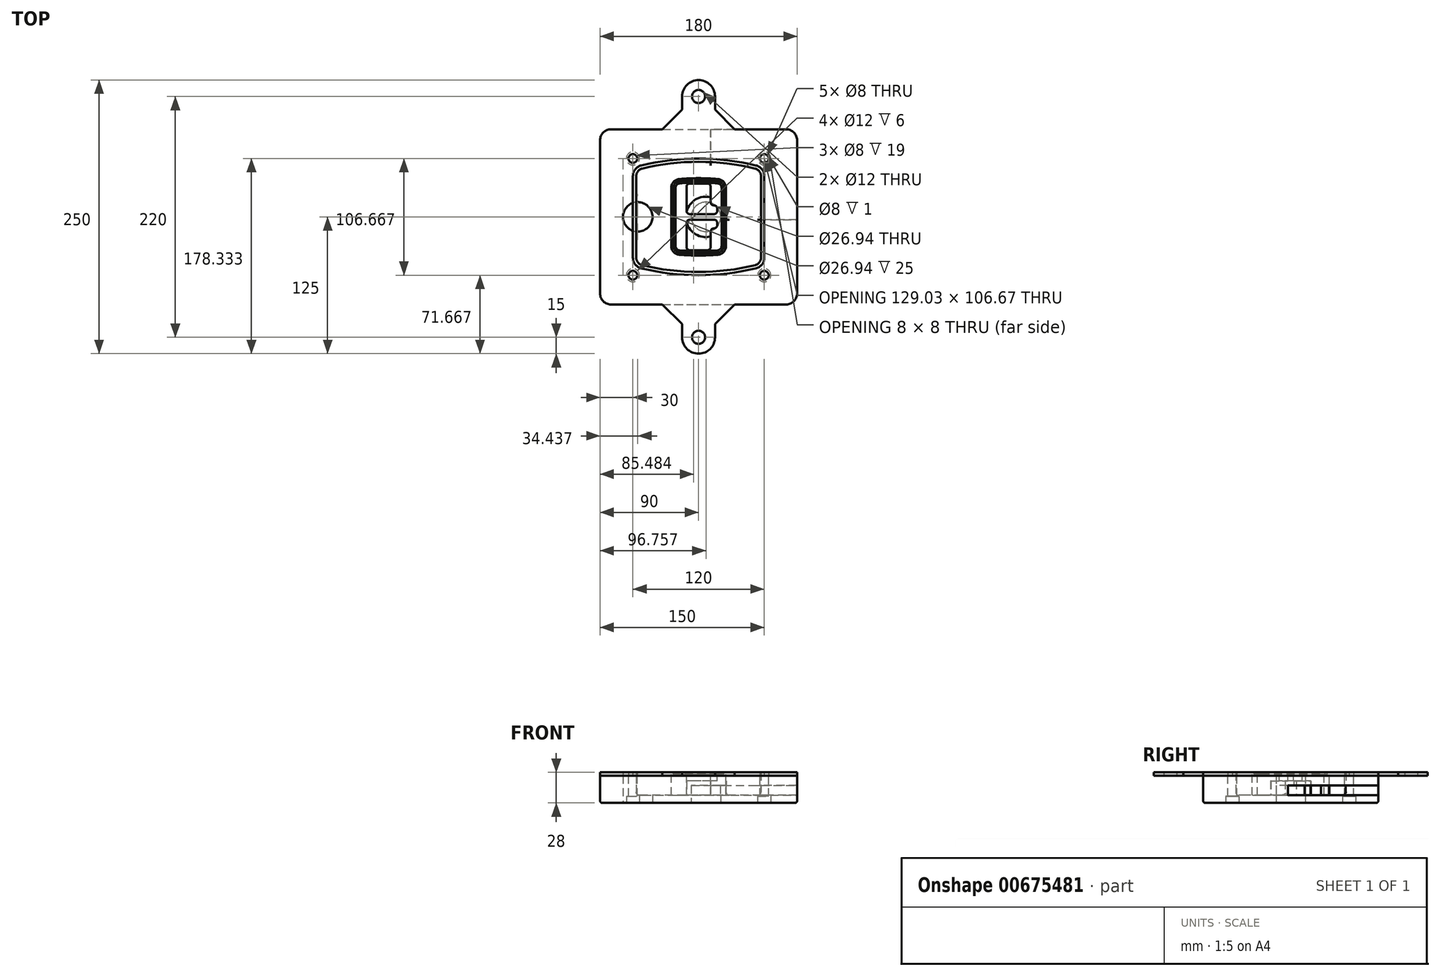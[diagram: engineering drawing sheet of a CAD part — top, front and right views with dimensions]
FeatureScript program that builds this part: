
annotation { "Feature Type Name" : "Feature", "Feature Type Description" : "" }
export const myFeature = defineFeature(function(context is Context, id is Id, definition is map)
    precondition{}
    {
        {
            var Q0;
            Q0=qCreatedBy(makeId("Top.planeOp"),FACE);
            var sketch = newSketch(context, id + "F0", { "sketchPlane" : qUnion([Q0])});
            skPoint(sketch, "E0.rect.middle", {"position": v(0, 0) * mm});
            skLineSegment(sketch, "E1.bottom", {"start": v(-80, -80) * mm, "end": v(80, -80) * mm});
            skLineSegment(sketch, "E1.top", {"start": v(-80, 80) * mm, "end": v(80, 80) * mm});
            skLineSegment(sketch, "E1.left", {"start": v(-90, -70) * mm, "end": v(-90, 70) * mm});
            skLineSegment(sketch, "E1.right", {"start": v(90, -70) * mm, "end": v(90, 70) * mm});
            skLineSegment(sketch, "E2", {"start": v(-90, 80) * mm, "end": v(90, -80) * mm, "construction": true});
            skLineSegment(sketch, "E3", {"start": v(90, 80) * mm, "end": v(-90, -80) * mm, "construction": true});
            skCircle(sketch, "E4", {"center": v(-60, 53.33) * mm, "radius": 4 * mm});
            skCircle(sketch, "E5", {"center": v(60, 53.33) * mm, "radius": 4 * mm});
            skCircle(sketch, "E6", {"center": v(60, -53.33) * mm, "radius": 4 * mm});
            skCircle(sketch, "E7", {"center": v(-60, -53.33) * mm, "radius": 4 * mm});
            skLineSegment(sketch, "E8", {"start": v(-60, 53.33) * mm, "end": v(60, 53.33) * mm, "construction": true});
            skLineSegment(sketch, "E9", {"start": v(60, 53.33) * mm, "end": v(60, -53.33) * mm, "construction": true});
            skLineSegment(sketch, "E10", {"start": v(60, -53.33) * mm, "end": v(-60, -53.33) * mm, "construction": true});
            skLineSegment(sketch, "E11", {"start": v(-60, -53.33) * mm, "end": v(-60, 53.33) * mm, "construction": true});
            skLineSegment(sketch, "E12", {"start": v(-60, 37.3) * mm, "end": v(-60, -37.3) * mm});
            skLineSegment(sketch, "E13", {"start": v(60, 37.3) * mm, "end": v(60, -37.3) * mm});
            skArc(sketch, "E14", {"start": v(52.38, 47.01) * mm, "mid": v(0, 53.33) * mm, "end": v(-52.38, 47.01) * mm});
            skArc(sketch, "E15", {"start": v(-52.38, -47.01) * mm, "mid": v(0, -53.33) * mm, "end": v(52.38, -47.01) * mm});
            skLineSegment(sketch, "E16", {"start": v(-60, 0) * mm, "end": v(60, 0) * mm, "construction": true});
            skPoint(sketch, "E17.visualSharp", {"position": v(-60, -45) * mm});
            skArc(sketch, "E17.filletArc", {"start": v(-60, -37.3) * mm, "mid": v(-57.87, -43.47) * mm, "end": v(-52.38, -47.01) * mm});
            skPoint(sketch, "E18.visualSharp", {"position": v(-60, 45) * mm});
            skArc(sketch, "E18.filletArc", {"start": v(-52.38, 47.01) * mm, "mid": v(-57.87, 43.47) * mm, "end": v(-60, 37.3) * mm});
            skPoint(sketch, "E19.visualSharp", {"position": v(60, 45) * mm});
            skArc(sketch, "E19.filletArc", {"start": v(60, 37.3) * mm, "mid": v(57.87, 43.47) * mm, "end": v(52.38, 47.01) * mm});
            skPoint(sketch, "E20.visualSharp", {"position": v(60, -45) * mm});
            skArc(sketch, "E20.filletArc", {"start": v(52.38, -47.01) * mm, "mid": v(57.87, -43.47) * mm, "end": v(60, -37.3) * mm});
            skPoint(sketch, "E21.visualSharp", {"position": v(-90, 80) * mm});
            skArc(sketch, "E21.filletArc", {"start": v(-80, 80) * mm, "mid": v(-87.07, 77.07) * mm, "end": v(-90, 70) * mm});
            skPoint(sketch, "E22.visualSharp", {"position": v(90, 80) * mm});
            skArc(sketch, "E22.filletArc", {"start": v(90, 70) * mm, "mid": v(87.07, 77.07) * mm, "end": v(80, 80) * mm});
            skPoint(sketch, "E23.visualSharp", {"position": v(90, -80) * mm});
            skArc(sketch, "E23.filletArc", {"start": v(80, -80) * mm, "mid": v(87.07, -77.07) * mm, "end": v(90, -70) * mm});
            skPoint(sketch, "E24.visualSharp", {"position": v(-90, -80) * mm});
            skArc(sketch, "E24.filletArc", {"start": v(-90, -70) * mm, "mid": v(-87.07, -77.07) * mm, "end": v(-80, -80) * mm});
            skArc(sketch, "E25.0", {"start": v(57, 37.3) * mm, "mid": v(55.5, 41.62) * mm, "end": v(51.67, 44.1) * mm});
            skLineSegment(sketch, "E25.1", {"start": v(57, 37.3) * mm, "end": v(57, -37.3) * mm});
            skArc(sketch, "E25.2", {"start": v(51.67, -44.1) * mm, "mid": v(55.5, -41.62) * mm, "end": v(57, -37.3) * mm});
            skArc(sketch, "E25.3", {"start": v(-51.67, -44.1) * mm, "mid": v(0, -50.33) * mm, "end": v(51.67, -44.1) * mm});
            skArc(sketch, "E25.4", {"start": v(-57, -37.3) * mm, "mid": v(-55.5, -41.62) * mm, "end": v(-51.67, -44.1) * mm});
            skArc(sketch, "E25.5", {"start": v(51.67, 44.1) * mm, "mid": v(0, 50.33) * mm, "end": v(-51.67, 44.1) * mm});
            skLineSegment(sketch, "E25.6", {"start": v(-57, 37.3) * mm, "end": v(-57, -37.3) * mm});
            skArc(sketch, "E25.7", {"start": v(-51.67, 44.1) * mm, "mid": v(-55.5, 41.62) * mm, "end": v(-57, 37.3) * mm});
            skArc(sketch, "E26.0", {"start": v(-53.33, 50.9) * mm, "mid": v(-61.01, 45.94) * mm, "end": v(-64, 37.3) * mm});
            skArc(sketch, "E26.1", {"start": v(53.33, 50.9) * mm, "mid": v(0, 57.33) * mm, "end": v(-53.33, 50.9) * mm});
            skArc(sketch, "E26.2", {"start": v(64, 37.3) * mm, "mid": v(61.01, 45.94) * mm, "end": v(53.33, 50.9) * mm});
            skLineSegment(sketch, "E26.3", {"start": v(64, 37.3) * mm, "end": v(64, -37.3) * mm});
            skArc(sketch, "E26.4", {"start": v(53.33, -50.9) * mm, "mid": v(61.01, -45.94) * mm, "end": v(64, -37.3) * mm});
            skLineSegment(sketch, "E26.5", {"start": v(-64, 37.3) * mm, "end": v(-64, -37.3) * mm});
            skArc(sketch, "E26.6", {"start": v(-53.33, -50.9) * mm, "mid": v(0, -57.33) * mm, "end": v(53.33, -50.9) * mm});
            skArc(sketch, "E26.7", {"start": v(-64, -37.3) * mm, "mid": v(-61.01, -45.94) * mm, "end": v(-53.33, -50.9) * mm});
            skSolve(sketch);
        }
        {
            var Q0;
            Q0=makeQuery(id+"F0.imprint","IMPRINT",FACE,{"disambiguationData":[TD([[makeQuery(id+"F0.imprint","IMPRINT",EDGE,{"derivedFrom":sQuery(id+"F0.wireOp",EDGE,"E1.bottom")}),1.0]])]});
            var Q1;
            Q1=makeQuery(id+"F0.imprint","IMPRINT",FACE,{"disambiguationData":[TD([[makeQuery(id+"F0.imprint","IMPRINT",EDGE,{"derivedFrom":sQuery(id+"F0.wireOp",EDGE,"E12")}),1.0]])]});
            var Q2;
            Q2=makeQuery(id+"F0.imprint","IMPRINT",FACE,{"disambiguationData":[TD([[makeQuery(id+"F0.imprint","IMPRINT",EDGE,{"derivedFrom":sQuery(id+"F0.wireOp",EDGE,"E25.0")}),1.0]])]});
            var Q3;
            Q3=makeQuery(id+"F0.imprint","IMPRINT",FACE,{"disambiguationData":[TD([[makeQuery(id+"F0.imprint","IMPRINT",EDGE,{"derivedFrom":sQuery(id+"F0.wireOp",EDGE,"E12")}),-1.0]])]});
            extrude(context, id + "F1", {"entities" : qUnion([Q0, Q1, Q2, Q3]), "oppositeDirection" : true, "depth" : 25 * mm});
        }
        {
            var Q0;
            Q0=makeQuery(id+"F0.imprint","IMPRINT",FACE,{"disambiguationData":[TD([[makeQuery(id+"F0.imprint","IMPRINT",EDGE,{"derivedFrom":sQuery(id+"F0.wireOp",EDGE,"E12")}),1.0]])]});
            extrude(context, id + "F2", {"entities" : qUnion([Q0]), "operationType" : NewBodyOperationType.ADD, "depth" : 3 * mm});
        }
        {
            var Q0;
            Q0=makeQuery(id+"F0.imprint","IMPRINT",FACE,{"disambiguationData":[TD([[makeQuery(id+"F0.imprint","IMPRINT",EDGE,{"derivedFrom":sQuery(id+"F0.wireOp",EDGE,"E25.0")}),1.0]])]});
            extrude(context, id + "F3", {"entities" : qUnion([Q0]), "operationType" : NewBodyOperationType.REMOVE, "oppositeDirection" : true, "depth" : 18 * mm});
        }
        {
            var Q0;
            Q0=makeQuery(id+"F2.opExtrude","CAP_FACE",FACE,{"disambiguationData":[OSD([sQuery(id+"F0.wireOp",EDGE,"E12"),sQuery(id+"F0.wireOp",EDGE,"E13"),sQuery(id+"F0.wireOp",EDGE,"E14"),sQuery(id+"F0.wireOp",EDGE,"E15"),sQuery(id+"F0.wireOp",EDGE,"E17.filletArc"),sQuery(id+"F0.wireOp",EDGE,"E18.filletArc"),sQuery(id+"F0.wireOp",EDGE,"E19.filletArc"),sQuery(id+"F0.wireOp",EDGE,"E20.filletArc"),sQuery(id+"F0.wireOp",EDGE,"E25.0"),sQuery(id+"F0.wireOp",EDGE,"E25.1"),sQuery(id+"F0.wireOp",EDGE,"E25.2"),sQuery(id+"F0.wireOp",EDGE,"E25.3"),sQuery(id+"F0.wireOp",EDGE,"E25.4"),sQuery(id+"F0.wireOp",EDGE,"E25.5"),sQuery(id+"F0.wireOp",EDGE,"E25.6"),sQuery(id+"F0.wireOp",EDGE,"E25.7")])],"isStart":false});
            var sketch = newSketch(context, id + "F4", { "sketchPlane" : qUnion([Q0])});
            skArc(sketch, "E27.0", {"start": v(-17.7, -34.56) * mm, "mid": v(0, -35.33) * mm, "end": v(17.7, -34.56) * mm});
            skArc(sketch, "E28.0", {"start": v(17.7, 34.56) * mm, "mid": v(0, 35.33) * mm, "end": v(-17.7, 34.56) * mm});
            skLineSegment(sketch, "E29", {"start": v(-25, 26.59) * mm, "end": v(-25, -26.59) * mm});
            skLineSegment(sketch, "E30", {"start": v(25, 26.59) * mm, "end": v(25, -26.59) * mm});
            skLineSegment(sketch, "E31", {"start": v(-25, 33.78) * mm, "end": v(25, 33.78) * mm, "construction": true});
            skLineSegment(sketch, "E32", {"start": v(-25, -33.78) * mm, "end": v(25, -33.78) * mm, "construction": true});
            skPoint(sketch, "E33.visualSharp", {"position": v(-25, 33.78) * mm});
            skArc(sketch, "E33.filletArc", {"start": v(-17.7, 34.56) * mm, "mid": v(-22.9, 32) * mm, "end": v(-25, 26.59) * mm});
            skPoint(sketch, "E34.visualSharp", {"position": v(25, 33.78) * mm});
            skArc(sketch, "E34.filletArc", {"start": v(25, 26.59) * mm, "mid": v(22.9, 32) * mm, "end": v(17.7, 34.56) * mm});
            skPoint(sketch, "E35.visualSharp", {"position": v(25, -33.78) * mm});
            skArc(sketch, "E35.filletArc", {"start": v(17.7, -34.56) * mm, "mid": v(22.9, -32) * mm, "end": v(25, -26.59) * mm});
            skPoint(sketch, "E36.visualSharp", {"position": v(-25, -33.78) * mm});
            skArc(sketch, "E36.filletArc", {"start": v(-25, -26.59) * mm, "mid": v(-22.9, -32) * mm, "end": v(-17.7, -34.56) * mm});
            skArc(sketch, "E37.0", {"start": v(51.67, 44.1) * mm, "mid": v(0, 50.33) * mm, "end": v(-51.67, 44.1) * mm});
            skArc(sketch, "E37.1", {"start": v(-51.67, 44.1) * mm, "mid": v(-55.5, 41.62) * mm, "end": v(-57, 37.3) * mm});
            skLineSegment(sketch, "E37.2", {"start": v(-57, 37.3) * mm, "end": v(-57, -37.3) * mm});
            skArc(sketch, "E37.3", {"start": v(-57, -37.3) * mm, "mid": v(-55.5, -41.62) * mm, "end": v(-51.67, -44.1) * mm});
            skArc(sketch, "E37.4", {"start": v(-51.67, -44.1) * mm, "mid": v(0, -50.33) * mm, "end": v(51.67, -44.1) * mm});
            skArc(sketch, "E37.5", {"start": v(51.67, -44.1) * mm, "mid": v(55.5, -41.62) * mm, "end": v(57, -37.3) * mm});
            skLineSegment(sketch, "E37.6", {"start": v(57, 37.3) * mm, "end": v(57, -37.3) * mm});
            skArc(sketch, "E37.7", {"start": v(57, 37.3) * mm, "mid": v(55.5, 41.62) * mm, "end": v(51.67, 44.1) * mm});
            skLineSegment(sketch, "E38.0", {"start": v(23, 26.59) * mm, "end": v(23, -26.59) * mm});
            skArc(sketch, "E38.1", {"start": v(17.53, -32.56) * mm, "mid": v(21.42, -30.64) * mm, "end": v(23, -26.59) * mm});
            skArc(sketch, "E38.2", {"start": v(-17.53, -32.56) * mm, "mid": v(0, -33.33) * mm, "end": v(17.53, -32.56) * mm});
            skArc(sketch, "E38.3", {"start": v(-23, -26.59) * mm, "mid": v(-21.42, -30.64) * mm, "end": v(-17.53, -32.56) * mm});
            skLineSegment(sketch, "E38.4", {"start": v(-23, 26.59) * mm, "end": v(-23, -26.59) * mm});
            skArc(sketch, "E38.5", {"start": v(23, 26.59) * mm, "mid": v(21.42, 30.64) * mm, "end": v(17.53, 32.56) * mm});
            skArc(sketch, "E38.6", {"start": v(-17.53, 32.56) * mm, "mid": v(-21.42, 30.64) * mm, "end": v(-23, 26.59) * mm});
            skArc(sketch, "E38.7", {"start": v(17.53, 32.56) * mm, "mid": v(0, 33.33) * mm, "end": v(-17.53, 32.56) * mm});
            skArc(sketch, "E39.0", {"start": v(21, 26.59) * mm, "mid": v(19.95, 29.29) * mm, "end": v(17.35, 30.57) * mm});
            skLineSegment(sketch, "E39.1", {"start": v(21, 26.59) * mm, "end": v(21, -26.59) * mm});
            skArc(sketch, "E39.2", {"start": v(17.35, -30.57) * mm, "mid": v(19.95, -29.29) * mm, "end": v(21, -26.59) * mm});
            skArc(sketch, "E39.3", {"start": v(-17.35, -30.57) * mm, "mid": v(0, -31.33) * mm, "end": v(17.35, -30.57) * mm});
            skArc(sketch, "E39.4", {"start": v(-21, -26.59) * mm, "mid": v(-19.95, -29.29) * mm, "end": v(-17.35, -30.57) * mm});
            skArc(sketch, "E39.5", {"start": v(17.35, 30.57) * mm, "mid": v(0, 31.33) * mm, "end": v(-17.35, 30.57) * mm});
            skLineSegment(sketch, "E39.6", {"start": v(-21, 26.59) * mm, "end": v(-21, -26.59) * mm});
            skArc(sketch, "E39.7", {"start": v(-17.35, 30.57) * mm, "mid": v(-19.95, 29.29) * mm, "end": v(-21, 26.59) * mm});
            skLineSegment(sketch, "E40", {"start": v(-25, 0) * mm, "end": v(25, 0) * mm, "construction": true});
            skLineSegment(sketch, "E41", {"start": v(-11, 5.5) * mm, "end": v(-11, 27.5) * mm});
            skLineSegment(sketch, "E42", {"start": v(-8, 30.5) * mm, "end": v(8, 30.5) * mm});
            skLineSegment(sketch, "E43", {"start": v(11, 27.5) * mm, "end": v(11, 13.5) * mm});
            skLineSegment(sketch, "E44", {"start": v(14, 10.5) * mm, "end": v(14, 10.5) * mm});
            skLineSegment(sketch, "E45", {"start": v(17, 7.5) * mm, "end": v(17, 5.5) * mm});
            skLineSegment(sketch, "E46", {"start": v(14, 2.5) * mm, "end": v(-8, 2.5) * mm});
            skPoint(sketch, "E47.visualSharp", {"position": v(-11, 30.5) * mm});
            skArc(sketch, "E47.filletArc", {"start": v(-8, 30.5) * mm, "mid": v(-10.12, 29.62) * mm, "end": v(-11, 27.5) * mm});
            skPoint(sketch, "E48.visualSharp", {"position": v(11, 30.5) * mm});
            skArc(sketch, "E48.filletArc", {"start": v(11, 27.5) * mm, "mid": v(10.12, 29.62) * mm, "end": v(8, 30.5) * mm});
            skPoint(sketch, "E49.visualSharp", {"position": v(11, 10.5) * mm});
            skArc(sketch, "E49.filletArc", {"start": v(11, 13.5) * mm, "mid": v(11.88, 11.38) * mm, "end": v(14, 10.5) * mm});
            skPoint(sketch, "E50.visualSharp", {"position": v(17, 10.5) * mm});
            skArc(sketch, "E50.filletArc", {"start": v(17, 7.5) * mm, "mid": v(16.12, 9.62) * mm, "end": v(14, 10.5) * mm});
            skPoint(sketch, "E51.visualSharp", {"position": v(17, 2.5) * mm});
            skArc(sketch, "E51.filletArc", {"start": v(14, 2.5) * mm, "mid": v(16.12, 3.38) * mm, "end": v(17, 5.5) * mm});
            skPoint(sketch, "E52.visualSharp", {"position": v(-11, 2.5) * mm});
            skArc(sketch, "E52.filletArc", {"start": v(-11, 5.5) * mm, "mid": v(-10.12, 3.38) * mm, "end": v(-8, 2.5) * mm});
            skLineSegment(sketch, "E53.0.MirrorCS", {"start": v(14, -2.5) * mm, "end": v(-8, -2.5) * mm});
            skArc(sketch, "E54.0.MirrorCS", {"start": v(-11, -5.5) * mm, "mid": v(-10.12, -3.38) * mm, "end": v(-8, -2.5) * mm});
            skLineSegment(sketch, "E55.0.MirrorCS", {"start": v(-11, -5.5) * mm, "end": v(-11, -27.5) * mm});
            skArc(sketch, "E56.0.MirrorCS", {"start": v(-8, -30.5) * mm, "mid": v(-10.12, -29.62) * mm, "end": v(-11, -27.5) * mm});
            skLineSegment(sketch, "E57.0.MirrorCS", {"start": v(-8, -30.5) * mm, "end": v(8, -30.5) * mm});
            skArc(sketch, "E58.0.MirrorCS", {"start": v(11, -27.5) * mm, "mid": v(10.12, -29.62) * mm, "end": v(8, -30.5) * mm});
            skLineSegment(sketch, "E59.0.MirrorCS", {"start": v(11, -27.5) * mm, "end": v(11, -13.5) * mm});
            skArc(sketch, "E60.0.MirrorCS", {"start": v(11, -13.5) * mm, "mid": v(11.88, -11.38) * mm, "end": v(14, -10.5) * mm});
            skArc(sketch, "E61.0.MirrorCS", {"start": v(17, -7.5) * mm, "mid": v(16.12, -9.62) * mm, "end": v(14, -10.5) * mm});
            skLineSegment(sketch, "E62.0.MirrorCS", {"start": v(17, -7.5) * mm, "end": v(17, -5.5) * mm});
            skArc(sketch, "E63.0.MirrorCS", {"start": v(14, -2.5) * mm, "mid": v(16.12, -3.38) * mm, "end": v(17, -5.5) * mm});
            skSolve(sketch);
        }
        {
            var Q0;
            Q0=makeQuery(id+"F4.imprint","IMPRINT",FACE,{"disambiguationData":[TD([[makeQuery(id+"F4.imprint","IMPRINT",EDGE,{"derivedFrom":sQuery(id+"F4.wireOp",EDGE,"E27.0")}),1.0]])]});
            var Q1;
            Q1=makeQuery(id+"F4.imprint","IMPRINT",FACE,{"disambiguationData":[TD([[makeQuery(id+"F4.imprint","IMPRINT",EDGE,{"derivedFrom":sQuery(id+"F4.wireOp",EDGE,"E38.0")}),-1.0]])]});
            var Q2;
            Q2=makeQuery(id+"F4.imprint","IMPRINT",FACE,{"disambiguationData":[TD([[makeQuery(id+"F4.imprint","IMPRINT",EDGE,{"derivedFrom":sQuery(id+"F4.wireOp",EDGE,"E39.0")}),1.0]])]});
            extrude(context, id + "F5", {"entities" : qUnion([Q0, Q1, Q2]), "operationType" : NewBodyOperationType.ADD, "endBound" : BoundingType.UP_TO_NEXT, "oppositeDirection" : true, "depth" : 25 * mm});
        }
        {
            var Q0;
            Q0=makeQuery(id+"F4.imprint","IMPRINT",FACE,{"disambiguationData":[TD([[makeQuery(id+"F4.imprint","IMPRINT",EDGE,{"derivedFrom":sQuery(id+"F4.wireOp",EDGE,"E38.0")}),-1.0]])]});
            extrude(context, id + "F6", {"entities" : qUnion([Q0]), "operationType" : NewBodyOperationType.REMOVE, "oppositeDirection" : true, "depth" : 2 * mm});
        }
        {
            var Q0;
            Q0=makeQuery(id+"F1.opExtrude","CAP_FACE",FACE,{"disambiguationData":[OSD([sQuery(id+"F0.wireOp",EDGE,"E1.bottom"),sQuery(id+"F0.wireOp",EDGE,"E1.top"),sQuery(id+"F0.wireOp",EDGE,"E1.left"),sQuery(id+"F0.wireOp",EDGE,"E1.right"),sQuery(id+"F0.wireOp",EDGE,"E4"),sQuery(id+"F0.wireOp",EDGE,"E5"),sQuery(id+"F0.wireOp",EDGE,"E6"),sQuery(id+"F0.wireOp",EDGE,"E7"),sQuery(id+"F0.wireOp",EDGE,"E21.filletArc"),sQuery(id+"F0.wireOp",EDGE,"E22.filletArc"),sQuery(id+"F0.wireOp",EDGE,"E23.filletArc"),sQuery(id+"F0.wireOp",EDGE,"E24.filletArc")])],"isStart":false});
            var sketch = newSketch(context, id + "F7", { "sketchPlane" : qUnion([Q0])});
            skCircle(sketch, "E64", {"center": v(6.76, 0) * mm, "radius": 13.47 * mm});
            skCircle(sketch, "E65", {"center": v(-55.56, 0) * mm, "radius": 13.47 * mm});
            skLineSegment(sketch, "E66", {"start": v(90, 0) * mm, "end": v(-90, 0) * mm});
            skCircle(sketch, "E67", {"center": v(6.76, 0) * mm, "radius": 18.47 * mm});
            skCircle(sketch, "E68", {"center": v(60, -53.33) * mm, "radius": 6 * mm});
            skCircle(sketch, "E69", {"center": v(-60, -53.33) * mm, "radius": 6 * mm});
            skCircle(sketch, "E70", {"center": v(-60, 53.33) * mm, "radius": 6 * mm});
            skCircle(sketch, "E71", {"center": v(60, 53.33) * mm, "radius": 6 * mm});
            skSolve(sketch);
        }
        {
            var Q0;
            {var subQ1=sQuery(id+"F7.wireOp",EDGE,"E66");var subQ4=sQuery(id+"F7.wireOp",EDGE,"E64");var subQ6=makeQuery(id+"F7.imprint","INTERSECT",VERTEX,{"disambiguationData":[OD(0.0)],"derivedFrom":[subQ4,subQ1]});Q0=makeQuery(id+"F7.imprint","IMPRINT",FACE,{"disambiguationData":[TD([[makeQuery(id+"F7.imprint","IMPRINT",EDGE,{"disambiguationData":[TD([[subQ6,-1.0]])],"derivedFrom":subQ4}),-1.0]])]});}
            var Q1;
            {var subQ0=sQuery(id+"F7.wireOp",EDGE,"E66");var subQ1=sQuery(id+"F7.wireOp",EDGE,"E64");var subQ3=makeQuery(id+"F7.imprint","INTERSECT",VERTEX,{"disambiguationData":[OD(0.0)],"derivedFrom":[subQ1,subQ0]});Q1=makeQuery(id+"F7.imprint","IMPRINT",FACE,{"disambiguationData":[TD([[makeQuery(id+"F7.imprint","IMPRINT",EDGE,{"disambiguationData":[TD([[subQ3,-1.0]])],"derivedFrom":subQ1}),1.0]])]});}
            var Q2;
            {var subQ0=sQuery(id+"F7.wireOp",EDGE,"E66");var subQ1=sQuery(id+"F7.wireOp",EDGE,"E64");var subQ3=makeQuery(id+"F7.imprint","INTERSECT",VERTEX,{"disambiguationData":[OD(0.0)],"derivedFrom":[subQ1,subQ0]});Q2=makeQuery(id+"F7.imprint","IMPRINT",FACE,{"disambiguationData":[TD([[makeQuery(id+"F7.imprint","IMPRINT",EDGE,{"disambiguationData":[TD([[subQ3,1.0]])],"derivedFrom":subQ1}),1.0]])]});}
            var Q3;
            {var subQ1=sQuery(id+"F7.wireOp",EDGE,"E66");var subQ4=sQuery(id+"F7.wireOp",EDGE,"E64");var subQ6=makeQuery(id+"F7.imprint","INTERSECT",VERTEX,{"disambiguationData":[OD(0.0)],"derivedFrom":[subQ4,subQ1]});Q3=makeQuery(id+"F7.imprint","IMPRINT",FACE,{"disambiguationData":[TD([[makeQuery(id+"F7.imprint","IMPRINT",EDGE,{"disambiguationData":[TD([[subQ6,1.0]])],"derivedFrom":subQ4}),-1.0]])]});}
            extrude(context, id + "F8", {"entities" : qUnion([Q0, Q1, Q2, Q3]), "operationType" : NewBodyOperationType.ADD, "oppositeDirection" : true, "depth" : 20 * mm});
        }
        {
            var Q0;
            {var subQ0=sQuery(id+"F7.wireOp",EDGE,"E66");var subQ1=sQuery(id+"F7.wireOp",EDGE,"E64");var subQ3=makeQuery(id+"F7.imprint","INTERSECT",VERTEX,{"disambiguationData":[OD(0.0)],"derivedFrom":[subQ1,subQ0]});Q0=makeQuery(id+"F7.imprint","IMPRINT",FACE,{"disambiguationData":[TD([[makeQuery(id+"F7.imprint","IMPRINT",EDGE,{"disambiguationData":[TD([[subQ3,-1.0]])],"derivedFrom":subQ1}),1.0]])]});}
            var Q1;
            {var subQ0=sQuery(id+"F7.wireOp",EDGE,"E66");var subQ1=sQuery(id+"F7.wireOp",EDGE,"E64");var subQ3=makeQuery(id+"F7.imprint","INTERSECT",VERTEX,{"disambiguationData":[OD(0.0)],"derivedFrom":[subQ1,subQ0]});Q1=makeQuery(id+"F7.imprint","IMPRINT",FACE,{"disambiguationData":[TD([[makeQuery(id+"F7.imprint","IMPRINT",EDGE,{"disambiguationData":[TD([[subQ3,1.0]])],"derivedFrom":subQ1}),1.0]])]});}
            extrude(context, id + "F9", {"entities" : qUnion([Q0, Q1]), "operationType" : NewBodyOperationType.REMOVE, "oppositeDirection" : true, "depth" : 16 * mm});
        }
        {
            var Q0;
            {var subQ0=sQuery(id+"F7.wireOp",EDGE,"E66");var subQ1=sQuery(id+"F7.wireOp",EDGE,"E65");var subQ3=makeQuery(id+"F7.imprint","INTERSECT",VERTEX,{"disambiguationData":[OD(0.0)],"derivedFrom":[subQ1,subQ0]});Q0=makeQuery(id+"F7.imprint","IMPRINT",FACE,{"disambiguationData":[TD([[makeQuery(id+"F7.imprint","IMPRINT",EDGE,{"disambiguationData":[TD([[subQ3,-1.0]])],"derivedFrom":subQ1}),1.0]])]});}
            var Q1;
            {var subQ0=sQuery(id+"F7.wireOp",EDGE,"E66");var subQ1=sQuery(id+"F7.wireOp",EDGE,"E65");var subQ3=makeQuery(id+"F7.imprint","INTERSECT",VERTEX,{"disambiguationData":[OD(0.0)],"derivedFrom":[subQ1,subQ0]});Q1=makeQuery(id+"F7.imprint","IMPRINT",FACE,{"disambiguationData":[TD([[makeQuery(id+"F7.imprint","IMPRINT",EDGE,{"disambiguationData":[TD([[subQ3,1.0]])],"derivedFrom":subQ1}),1.0]])]});}
            extrude(context, id + "F10", {"entities" : qUnion([Q0, Q1]), "operationType" : NewBodyOperationType.REMOVE, "oppositeDirection" : true, "depth" : 25 * mm});
        }
        {
            var Q0;
            Q0=makeQuery(id+"F7.imprint","IMPRINT",FACE,{"disambiguationData":[TD([[makeQuery(id+"F7.imprint","IMPRINT",EDGE,{"derivedFrom":sQuery(id+"F7.wireOp",EDGE,"E68")}),1.0]])]});
            var Q1;
            Q1=makeQuery(id+"F7.imprint","IMPRINT",FACE,{"disambiguationData":[TD([[makeQuery(id+"F7.imprint","IMPRINT",EDGE,{"derivedFrom":makeQuery(id+"F1.opExtrude","CAP_EDGE",EDGE,{"disambiguationData":[OSD([sQuery(id+"F0.wireOp",EDGE,"E5")])],"isStart":false})}),-1.0]])]});
            var Q2;
            Q2=makeQuery(id+"F7.imprint","IMPRINT",FACE,{"disambiguationData":[TD([[makeQuery(id+"F7.imprint","IMPRINT",EDGE,{"derivedFrom":sQuery(id+"F7.wireOp",EDGE,"E69")}),1.0]])]});
            var Q3;
            Q3=makeQuery(id+"F7.imprint","IMPRINT",FACE,{"disambiguationData":[TD([[makeQuery(id+"F7.imprint","IMPRINT",EDGE,{"derivedFrom":makeQuery(id+"F1.opExtrude","CAP_EDGE",EDGE,{"disambiguationData":[OSD([sQuery(id+"F0.wireOp",EDGE,"E4")])],"isStart":false})}),-1.0]])]});
            var Q4;
            Q4=makeQuery(id+"F7.imprint","IMPRINT",FACE,{"disambiguationData":[TD([[makeQuery(id+"F7.imprint","IMPRINT",EDGE,{"derivedFrom":sQuery(id+"F7.wireOp",EDGE,"E70")}),1.0]])]});
            var Q5;
            Q5=makeQuery(id+"F7.imprint","IMPRINT",FACE,{"disambiguationData":[TD([[makeQuery(id+"F7.imprint","IMPRINT",EDGE,{"derivedFrom":makeQuery(id+"F1.opExtrude","CAP_EDGE",EDGE,{"disambiguationData":[OSD([sQuery(id+"F0.wireOp",EDGE,"E7")])],"isStart":false})}),-1.0]])]});
            var Q6;
            Q6=makeQuery(id+"F7.imprint","IMPRINT",FACE,{"disambiguationData":[TD([[makeQuery(id+"F7.imprint","IMPRINT",EDGE,{"derivedFrom":sQuery(id+"F7.wireOp",EDGE,"E71")}),1.0]])]});
            var Q7;
            Q7=makeQuery(id+"F7.imprint","IMPRINT",FACE,{"disambiguationData":[TD([[makeQuery(id+"F7.imprint","IMPRINT",EDGE,{"derivedFrom":makeQuery(id+"F1.opExtrude","CAP_EDGE",EDGE,{"disambiguationData":[OSD([sQuery(id+"F0.wireOp",EDGE,"E6")])],"isStart":false})}),-1.0]])]});
            extrude(context, id + "F11", {"entities" : qUnion([Q0, Q1, Q2, Q3, Q4, Q5, Q6, Q7]), "operationType" : NewBodyOperationType.REMOVE, "oppositeDirection" : true, "depth" : 6 * mm});
        }
        {
            var Q0;
            Q0=makeQuery(id+"F9.boolean.opBoolean","COPY",FACE,{"derivedFrom":makeQuery(id+"F9.opExtrude","CAP_FACE",FACE,{"disambiguationData":[OSD([sQuery(id+"F7.wireOp",EDGE,"E64")])],"isStart":false})});
            var sketch = newSketch(context, id + "F12", { "sketchPlane" : qUnion([Q0])});
            skArc(sketch, "E72.0", {"start": v(11, -88.19) * mm, "mid": v(97.1, -83.6) * mm, "end": v(92.5, 2.5) * mm});
            skLineSegment(sketch, "E72.1", {"start": v(11, -17.97) * mm, "end": v(11, -17.97) * mm});
            skLineSegment(sketch, "E73", {"start": v(92.5, -105.13) * mm, "end": v(102.3, -105.13) * mm});
            skLineSegment(sketch, "E74.0", {"start": v(92.5, 2.5) * mm, "end": v(14, 2.5) * mm});
            skArc(sketch, "E74.1", {"start": v(14, 2.5) * mm, "mid": v(16.12, 3.38) * mm, "end": v(17, 5.5) * mm});
            skLineSegment(sketch, "E74.2", {"start": v(17, 7.5) * mm, "end": v(17, 5.5) * mm});
            skArc(sketch, "E74.3", {"start": v(17, 7.5) * mm, "mid": v(16.12, 9.62) * mm, "end": v(14, 10.5) * mm});
            skArc(sketch, "E74.4", {"start": v(11, 13.5) * mm, "mid": v(11.88, 11.38) * mm, "end": v(14, 10.5) * mm});
            skLineSegment(sketch, "E74.5", {"start": v(11, 13.5) * mm, "end": v(11, -88.19) * mm});
            skLineSegment(sketch, "E74.7", {"start": v(92.5, -2.5) * mm, "end": v(14, -2.5) * mm});
            skArc(sketch, "E74.8", {"start": v(14, -2.5) * mm, "mid": v(16.12, -3.38) * mm, "end": v(17, -5.5) * mm});
            skLineSegment(sketch, "E74.9", {"start": v(17, -7.5) * mm, "end": v(17, -5.5) * mm});
            skArc(sketch, "E74.10", {"start": v(17, -7.5) * mm, "mid": v(16.12, -9.62) * mm, "end": v(14, -10.5) * mm});
            skArc(sketch, "E74.11", {"start": v(11, -13.5) * mm, "mid": v(11.88, -11.38) * mm, "end": v(14, -10.5) * mm});
            skLineSegment(sketch, "E74.12", {"start": v(11, -17.97) * mm, "end": v(11, -13.5) * mm});
            skPoint(sketch, "E75.orphan", {"position": v(11, -27.5) * mm});
            skPoint(sketch, "E76.orphan", {"position": v(-8, -2.5) * mm});
            skPoint(sketch, "E77.orphan", {"position": v(-8, 2.5) * mm});
            skPoint(sketch, "E78.orphan", {"position": v(11, 27.5) * mm});
            skSolve(sketch);
        }
        {
            var Q0;
            {var subQ7=sQuery(id+"F12.wireOp",EDGE,"E72.0");var subQ14=sQuery(id+"F12.wireOp",EDGE,"E72.1");var subQ16=sQuery(id+"F12.wireOp",EDGE,"E74.1");var subQ18=sQuery(id+"F12.wireOp",EDGE,"E74.8");Q0=qUnion([makeQuery(id+"F12.imprint","IMPRINT",FACE,{"disambiguationData":[TD([[makeQuery(id+"F12.imprint","IMPRINT",EDGE,{"derivedFrom":subQ7}),1.0]])]}),makeQuery(id+"F12.imprint","IMPRINT",FACE,{"disambiguationData":[TD([[makeQuery(id+"F12.imprint","IMPRINT",EDGE,{"derivedFrom":subQ14}),1.0]])]}),makeQuery(id+"F12.imprint","IMPRINT",FACE,{"disambiguationData":[TD([[makeQuery(id+"F12.imprint","IMPRINT",EDGE,{"derivedFrom":subQ16}),1.0]])]}),makeQuery(id+"F12.imprint","IMPRINT",FACE,{"disambiguationData":[TD([[makeQuery(id+"F12.imprint","IMPRINT",EDGE,{"derivedFrom":subQ18}),-1.0]])]})]);}
            var Q1;
            Q1=makeQuery(id+"F5.boolean.opBoolean","SPLIT",FACE,{"disambiguationData":[TD([makeQuery(id+"F5.opExtrude","SWEPT_FACE",FACE,{"disambiguationData":[OSD([sQuery(id+"F4.wireOp",EDGE,"E41")])]})])],"derivedFrom":makeQuery(id+"F3.boolean.opBoolean","COPY",FACE,{"derivedFrom":makeQuery(id+"F3.opExtrude","CAP_FACE",FACE,{"disambiguationData":[OSD([sQuery(id+"F0.wireOp",EDGE,"E25.0"),sQuery(id+"F0.wireOp",EDGE,"E25.1"),sQuery(id+"F0.wireOp",EDGE,"E25.2"),sQuery(id+"F0.wireOp",EDGE,"E25.3"),sQuery(id+"F0.wireOp",EDGE,"E25.4"),sQuery(id+"F0.wireOp",EDGE,"E25.5"),sQuery(id+"F0.wireOp",EDGE,"E25.6"),sQuery(id+"F0.wireOp",EDGE,"E25.7")])],"isStart":false})})});
            extrude(context, id + "F13", {"entities" : qUnion([Q0]), "operationType" : NewBodyOperationType.REMOVE, "endBound" : BoundingType.UP_TO_SURFACE, "endBoundEntityFace" : qUnion([Q1]), "depth" : 25 * mm});
        }
        {
            var Q0;
            Q0=makeQuery(id+"F3.boolean.opBoolean","COPY",EDGE,{"derivedFrom":makeQuery(id+"F3.opExtrude","CAP_EDGE",EDGE,{"disambiguationData":[OSD([sQuery(id+"F0.wireOp",EDGE,"E25.6")])],"isStart":false})});
            var Q1;
            Q1=makeQuery(id+"F8.boolean.opBoolean","INTERSECT",EDGE,{"derivedFrom":[makeQuery(id+"F5.opExtrude","SWEPT_FACE",FACE,{"disambiguationData":[OSD([sQuery(id+"F4.wireOp",EDGE,"E30")])]}),makeQuery(id+"F8.opExtrude","CAP_FACE",FACE,{"disambiguationData":[OSD([sQuery(id+"F7.wireOp",EDGE,"E67")])],"isStart":false})]});
            var Q2;
            Q2=makeQuery(id+"F8.boolean.opBoolean","INTERSECT",EDGE,{"disambiguationData":[OD(1.0)],"derivedFrom":[makeQuery(id+"F5.opExtrude","SWEPT_FACE",FACE,{"disambiguationData":[OSD([sQuery(id+"F4.wireOp",EDGE,"E30")])]}),makeQuery(id+"F8.opExtrude","SWEPT_FACE",FACE,{"disambiguationData":[OSD([sQuery(id+"F7.wireOp",EDGE,"E67")])]})]});
            var Q3;
            {var subQ0=makeQuery(id+"F3.boolean.opBoolean","COPY",FACE,{"derivedFrom":makeQuery(id+"F3.opExtrude","CAP_FACE",FACE,{"disambiguationData":[OSD([sQuery(id+"F0.wireOp",EDGE,"E25.0"),sQuery(id+"F0.wireOp",EDGE,"E25.1"),sQuery(id+"F0.wireOp",EDGE,"E25.2"),sQuery(id+"F0.wireOp",EDGE,"E25.3"),sQuery(id+"F0.wireOp",EDGE,"E25.4"),sQuery(id+"F0.wireOp",EDGE,"E25.5"),sQuery(id+"F0.wireOp",EDGE,"E25.6"),sQuery(id+"F0.wireOp",EDGE,"E25.7")])],"isStart":false})});var subQ1=sQuery(id+"F4.wireOp",EDGE,"E30");Q3=makeQuery(id+"F8.boolean.opBoolean","SPLIT",EDGE,{"disambiguationData":[TD([makeQuery(id+"F5.opExtrude","SWEPT_FACE",FACE,{"disambiguationData":[OSD([sQuery(id+"F4.wireOp",EDGE,"E35.filletArc")])]})])],"derivedFrom":makeQuery(id+"F5.opExtrude","TWEAK_EDGE",EDGE,{"derivedFrom":[subQ0,makeQuery(id+"F4.imprint","IMPRINT",EDGE,{"derivedFrom":subQ1})]})});}
            var Q4;
            {var subQ0=sQuery(id+"F0.wireOp",EDGE,"E25.0");var subQ1=sQuery(id+"F0.wireOp",EDGE,"E25.1");var subQ2=sQuery(id+"F0.wireOp",EDGE,"E25.2");var subQ3=sQuery(id+"F0.wireOp",EDGE,"E25.3");var subQ4=sQuery(id+"F0.wireOp",EDGE,"E25.4");var subQ5=sQuery(id+"F0.wireOp",EDGE,"E25.5");var subQ6=sQuery(id+"F0.wireOp",EDGE,"E25.6");var subQ7=sQuery(id+"F0.wireOp",EDGE,"E25.7");Q4=makeQuery(id+"F8.boolean.opBoolean","INTERSECT",EDGE,{"derivedFrom":[makeQuery(id+"F5.boolean.opBoolean","SPLIT",FACE,{"disambiguationData":[TD([makeQuery(id+"F2.opExtrude","SWEPT_FACE",FACE,{"disambiguationData":[OSD([subQ0])]})])],"derivedFrom":makeQuery(id+"F3.boolean.opBoolean","COPY",FACE,{"derivedFrom":makeQuery(id+"F3.opExtrude","CAP_FACE",FACE,{"disambiguationData":[OSD([subQ0,subQ1,subQ2,subQ3,subQ4,subQ5,subQ6,subQ7])],"isStart":false})})}),makeQuery(id+"F8.opExtrude","SWEPT_FACE",FACE,{"disambiguationData":[OSD([sQuery(id+"F7.wireOp",EDGE,"E67")])]})]});}
            var Q5;
            Q5=makeQuery(id+"F8.boolean.opBoolean","INTERSECT",EDGE,{"disambiguationData":[OD(0.0)],"derivedFrom":[makeQuery(id+"F5.opExtrude","SWEPT_FACE",FACE,{"disambiguationData":[OSD([sQuery(id+"F4.wireOp",EDGE,"E30")])]}),makeQuery(id+"F8.opExtrude","SWEPT_FACE",FACE,{"disambiguationData":[OSD([sQuery(id+"F7.wireOp",EDGE,"E67")])]})]});
            fillet(context, id + "F14", {"entities" : qUnion([Q0, Q1, Q2, Q3, Q4, Q5]), "radius" : 3 * mm, "tangentPropagation" : true, "allowEdgeOverflow" : false});
        }
        {
            var Q0;
            Q0=makeQuery(id+"F1.opExtrude","CAP_EDGE",EDGE,{"disambiguationData":[OSD([sQuery(id+"F0.wireOp",EDGE,"E1.bottom")])],"isStart":false});
            fillet(context, id + "F15", {"entities" : qUnion([Q0]), "radius" : 2 * mm, "tangentPropagation" : true, "allowEdgeOverflow" : false});
        }
        {
            var Q0;
            {var subQ0=sQuery(id+"F0.wireOp",EDGE,"E21.filletArc");var subQ1=sQuery(id+"F0.wireOp",EDGE,"E7");var subQ2=sQuery(id+"F0.wireOp",EDGE,"E6");var subQ3=sQuery(id+"F0.wireOp",EDGE,"E5");var subQ4=sQuery(id+"F0.wireOp",EDGE,"E4");var subQ5=sQuery(id+"F0.wireOp",EDGE,"E22.filletArc");var subQ6=sQuery(id+"F0.wireOp",EDGE,"E1.bottom");var subQ7=sQuery(id+"F0.wireOp",EDGE,"E1.right");var subQ8=sQuery(id+"F0.wireOp",EDGE,"E1.top");var subQ9=sQuery(id+"F0.wireOp",EDGE,"E1.left");var subQ10=sQuery(id+"F0.wireOp",EDGE,"E23.filletArc");var subQ11=sQuery(id+"F0.wireOp",EDGE,"E24.filletArc");Q0=makeQuery(id+"F2.boolean.opBoolean","SPLIT",FACE,{"disambiguationData":[TD([makeQuery(id+"F1.opExtrude","SWEPT_FACE",FACE,{"disambiguationData":[OSD([subQ6])]})])],"derivedFrom":makeQuery(id+"F1.opExtrude","CAP_FACE",FACE,{"disambiguationData":[OSD([subQ6,subQ8,subQ9,subQ7,subQ4,subQ3,subQ2,subQ1,subQ0,subQ5,subQ10,subQ11])],"isStart":true})});}
            var sketch = newSketch(context, id + "F16", { "sketchPlane" : qUnion([Q0])});
            skPoint(sketch, "E79", {"position": v(0, 80) * mm});
            skLineSegment(sketch, "E80", {"start": v(0, 80) * mm, "end": v(0, 110) * mm, "construction": true});
            skCircle(sketch, "E81", {"center": v(0, 110) * mm, "radius": 6 * mm});
            skArc(sketch, "E82", {"start": v(15, 110) * mm, "mid": v(0, 125) * mm, "end": v(-15, 110) * mm});
            skLineSegment(sketch, "E83", {"start": v(-15, 110) * mm, "end": v(-15, 98) * mm});
            skLineSegment(sketch, "E84", {"start": v(15, 110) * mm, "end": v(15, 98) * mm});
            skLineSegment(sketch, "E85", {"start": v(-15, 98) * mm, "end": v(-33, 80) * mm});
            skLineSegment(sketch, "E86", {"start": v(15, 98) * mm, "end": v(33, 80) * mm});
            skLineSegment(sketch, "E87", {"start": v(-90, 0) * mm, "end": v(90, 0) * mm, "construction": true});
            skLineSegment(sketch, "E88.MirrorCS", {"start": v(0, -80) * mm, "end": v(0, -110) * mm, "construction": true});
            skLineSegment(sketch, "E89.MirrorCS", {"start": v(15, -98) * mm, "end": v(33, -80) * mm});
            skCircle(sketch, "E90.MirrorC", {"center": v(0, -110) * mm, "radius": 6 * mm});
            skLineSegment(sketch, "E91.MirrorCS", {"start": v(15, -110) * mm, "end": v(15, -98) * mm});
            skLineSegment(sketch, "E92.MirrorCS", {"start": v(-15, -110) * mm, "end": v(-15, -98) * mm});
            skLineSegment(sketch, "E93.MirrorCS", {"start": v(-15, -98) * mm, "end": v(-33, -80) * mm});
            skArc(sketch, "E94.MirrorCS", {"start": v(15, -110) * mm, "mid": v(0, -125) * mm, "end": v(-15, -110) * mm});
            skPoint(sketch, "E95.MirrorP", {"position": v(0, -80) * mm});
            skSolve(sketch);
        }
        {
            var Q0;
            Q0=makeQuery(id+"F16.imprint","IMPRINT",FACE,{"disambiguationData":[TD([[makeQuery(id+"F16.imprint","IMPRINT",EDGE,{"derivedFrom":sQuery(id+"F16.wireOp",EDGE,"E81")}),-1.0]])]});
            var Q1;
            {var subQ0=sQuery(id+"F16.wireOp",EDGE,"E89.MirrorCS");Q1=makeQuery(id+"F16.imprint","IMPRINT",FACE,{"disambiguationData":[TD([[makeQuery(id+"F16.imprint","IMPRINT",EDGE,{"derivedFrom":subQ0}),1.0]])]});}
            var Q2;
            Q2=makeQuery(id+"F16.imprint","IMPRINT",FACE,{"disambiguationData":[TD([[makeQuery(id+"F16.imprint","IMPRINT",EDGE,{"derivedFrom":makeQuery(id+"F1.opExtrude","CAP_EDGE",EDGE,{"disambiguationData":[OSD([sQuery(id+"F0.wireOp",EDGE,"E1.left")])],"isStart":true})}),-1.0]])]});
            var Q3;
            Q3=makeQuery(id+"F2.opExtrude","CAP_FACE",FACE,{"disambiguationData":[OSD([sQuery(id+"F0.wireOp",EDGE,"E12"),sQuery(id+"F0.wireOp",EDGE,"E13"),sQuery(id+"F0.wireOp",EDGE,"E14"),sQuery(id+"F0.wireOp",EDGE,"E15"),sQuery(id+"F0.wireOp",EDGE,"E17.filletArc"),sQuery(id+"F0.wireOp",EDGE,"E18.filletArc"),sQuery(id+"F0.wireOp",EDGE,"E19.filletArc"),sQuery(id+"F0.wireOp",EDGE,"E20.filletArc"),sQuery(id+"F0.wireOp",EDGE,"E25.0"),sQuery(id+"F0.wireOp",EDGE,"E25.1"),sQuery(id+"F0.wireOp",EDGE,"E25.2"),sQuery(id+"F0.wireOp",EDGE,"E25.3"),sQuery(id+"F0.wireOp",EDGE,"E25.4"),sQuery(id+"F0.wireOp",EDGE,"E25.5"),sQuery(id+"F0.wireOp",EDGE,"E25.6"),sQuery(id+"F0.wireOp",EDGE,"E25.7")])],"isStart":false});
            extrude(context, id + "F17", {"entities" : qUnion([Q0, Q1, Q2]), "endBound" : BoundingType.UP_TO_SURFACE, "depth" : 25 * mm, "endBoundEntityFace" : qUnion([Q3]), "offsetDistance" : 25 * mm});
        }
    });
